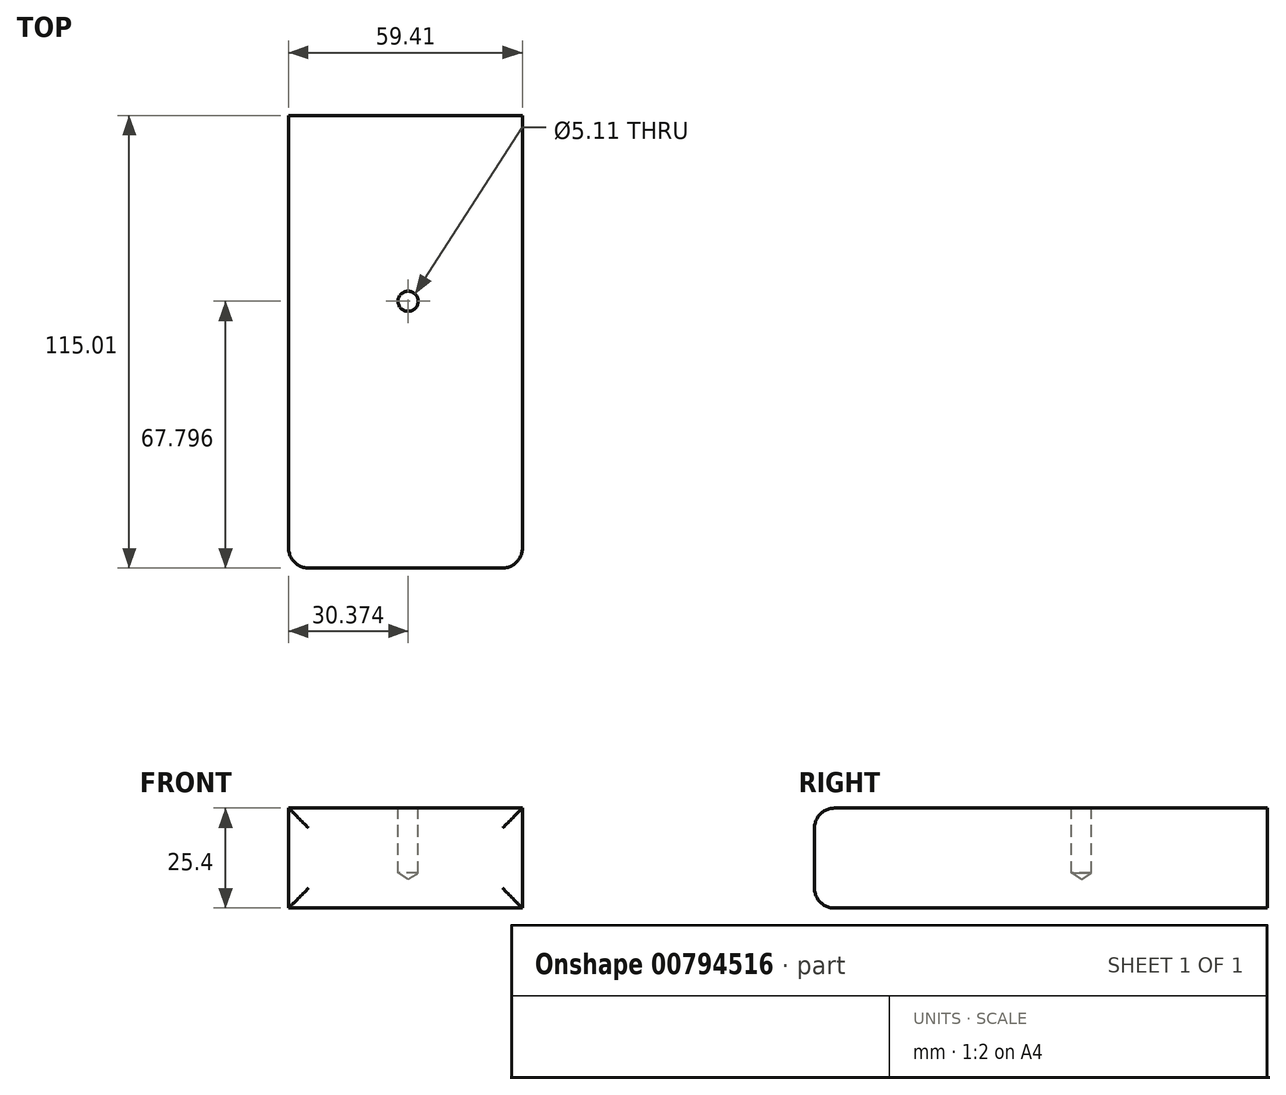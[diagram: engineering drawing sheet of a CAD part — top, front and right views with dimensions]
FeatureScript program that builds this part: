
annotation { "Feature Type Name" : "Feature", "Feature Type Description" : "" }
export const myFeature = defineFeature(function(context is Context, id is Id, definition is map)
    precondition{}
    {
        {
            var Q0;
            Q0=qCreatedBy(makeId("Top.planeOp"),FACE);
            var sketch = newSketch(context, id + "F0", { "sketchPlane" : qUnion([Q0])});
            skLineSegment(sketch, "E0.bottom", {"start": v(-44.07, -46.13) * mm, "end": v(15.34, -46.13) * mm});
            skLineSegment(sketch, "E0.top", {"start": v(-44.07, 68.88) * mm, "end": v(15.34, 68.88) * mm});
            skLineSegment(sketch, "E0.left", {"start": v(-44.07, -46.13) * mm, "end": v(-44.07, 68.88) * mm});
            skLineSegment(sketch, "E0.right", {"start": v(15.34, -46.13) * mm, "end": v(15.34, 68.88) * mm});
            skSolve(sketch);
        }
        {
            var Q0;
            Q0=makeQuery(id+"F0.imprint","IMPRINT",FACE,{"disambiguationData":[TD([[makeQuery(id+"F0.imprint","IMPRINT",EDGE,{"derivedFrom":sQuery(id+"F0.wireOp",EDGE,"E0.bottom")}),1.0]])]});
            extrude(context, id + "F1", {"entities" : qUnion([Q0]), "depth" : 25.4 * mm, "offsetDistance" : 25.4 * mm});
        }
        {
            var Q0;
            Q0=makeQuery(id+"F1.opExtrude","SWEPT_EDGE",EDGE,{"disambiguationData":[OSD([sQuery(id+"F0.wireOp",EDGE,"E0.bottom"),sQuery(id+"F0.wireOp",EDGE,"E0.left")])]});
            var Q1;
            Q1=makeQuery(id+"F1.opExtrude","CAP_EDGE",EDGE,{"disambiguationData":[OSD([sQuery(id+"F0.wireOp",EDGE,"E0.bottom")])],"isStart":false});
            var Q2;
            Q2=makeQuery(id+"F1.opExtrude","SWEPT_EDGE",EDGE,{"disambiguationData":[OSD([sQuery(id+"F0.wireOp",EDGE,"E0.bottom"),sQuery(id+"F0.wireOp",EDGE,"E0.right")])]});
            var Q3;
            Q3=makeQuery(id+"F1.opExtrude","CAP_EDGE",EDGE,{"disambiguationData":[OSD([sQuery(id+"F0.wireOp",EDGE,"E0.bottom")])],"isStart":true});
            fillet(context, id + "F2", {"entities" : qUnion([Q0, Q1, Q2, Q3]), "radius" : 5.08 * mm, "tangentPropagation" : true, "allowEdgeOverflow" : false});
        }
        {
            var Q0;
            Q0=makeQuery(id+"F1.opExtrude","CAP_FACE",FACE,{"disambiguationData":[OSD([sQuery(id+"F0.wireOp",EDGE,"E0.bottom"),sQuery(id+"F0.wireOp",EDGE,"E0.top"),sQuery(id+"F0.wireOp",EDGE,"E0.left"),sQuery(id+"F0.wireOp",EDGE,"E0.right")])],"isStart":false});
            var sketch = newSketch(context, id + "F3", { "sketchPlane" : qUnion([Q0])});
            skCircle(sketch, "E1", {"center": v(-13.7, 21.67) * mm, "radius": 17.02 * mm});
            skSolve(sketch);
        }
        {
            var Q0;
            Q0=sQuery(id+"F3.wireOp",VERTEX,"E1.center");
            var Q1;
            Q1=makeQuery(id+"F1.opExtrude","SWEPT_BODY",BODY,{"disambiguationData":[OSD([sQuery(id+"F0.wireOp",EDGE,"E0.bottom"),sQuery(id+"F0.wireOp",EDGE,"E0.top"),sQuery(id+"F0.wireOp",EDGE,"E0.left"),sQuery(id+"F0.wireOp",EDGE,"E0.right")])]});
            hole(context, id + "F4", {"style" : HoleStyle.SIMPLE, "endStyle" : HoleEndStyle.BLIND, "standardTappedOrClearance" : lookupTablePath({ "standard" : "ANSI", "engagement" : "75%", "pitch" : "20 tpi", "size" : "1/4", "type" : "Tapped" }), "standardBlindInLast" : lookupTablePath({ "standard" : "ANSI", "engagement" : "75%", "pitch" : "20 tpi", "size" : "1/4", "type" : "Tapped" }), "holeDiameter" : 5.1 * mm, "majorDiameter" : 6.35 * mm, "showTappedDepth" : true, "holeDepth" : 16.5 * mm, "isTappedThrough" : true, "tappedDepth" : 12.7 * mm, "tapClearance" : 3, "startFromSketch" : true, "locations" : qUnion([Q0]), "scope" : qUnion([Q1])});
        }
    });
